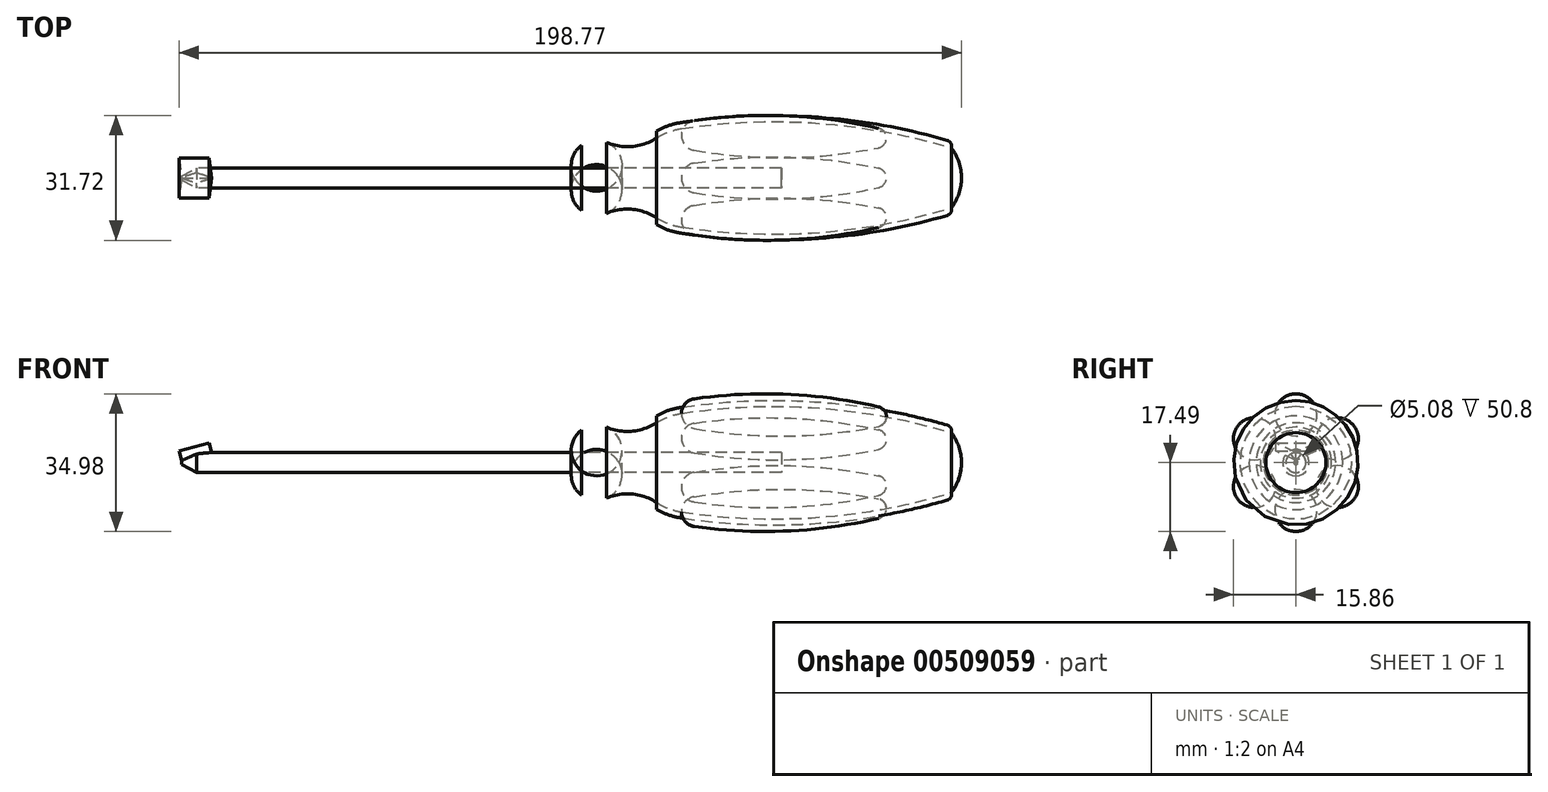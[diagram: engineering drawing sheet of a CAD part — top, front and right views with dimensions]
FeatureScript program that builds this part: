
annotation { "Feature Type Name" : "Feature", "Feature Type Description" : "" }
export const myFeature = defineFeature(function(context is Context, id is Id, definition is map)
    precondition{}
    {
        {
            var Q0;
            Q0=qCreatedBy(makeId("Front.planeOp"),FACE);
            var sketch = newSketch(context, id + "F0", { "sketchPlane" : qUnion([Q0])});
            skLineSegment(sketch, "E0", {"start": v(-101.6, 0) * mm, "end": v(96.52, 0) * mm});
            skLineSegment(sketch, "E1", {"start": v(96.52, 0) * mm, "end": v(117.55, 0) * mm, "construction": true});
            skLineSegment(sketch, "E2", {"start": v(50.8, 2.54) * mm, "end": v(-97.8, 2.54) * mm});
            skLineSegment(sketch, "E3", {"start": v(-101.6, 0.5) * mm, "end": v(-101.6, 0) * mm});
            skLineSegment(sketch, "E4", {"start": v(0, 2.54) * mm, "end": v(0, 8.25) * mm});
            skArc(sketch, "E5", {"start": v(6.35, 9.02) * mm, "mid": v(3.07, 9.48) * mm, "end": v(0, 8.25) * mm});
            skArc(sketch, "E6", {"start": v(6.35, 9.02) * mm, "mid": v(12.84, 7.99) * mm, "end": v(19.05, 10.11) * mm});
            skArc(sketch, "E7", {"start": v(25.4, 12.52) * mm, "mid": v(22.1, 11.65) * mm, "end": v(19.05, 10.11) * mm});
            skArc(sketch, "E8", {"start": v(93.98, 7.62) * mm, "mid": v(59.96, 13.9) * mm, "end": v(25.4, 12.52) * mm});
            skArc(sketch, "E9", {"start": v(96.52, 0) * mm, "mid": v(95.87, 4.02) * mm, "end": v(93.98, 7.62) * mm});
            skArc(sketch, "E10.0", {"start": v(25.17, 14.02) * mm, "mid": v(22.01, 13.24) * mm, "end": v(19.05, 11.9) * mm});
            skArc(sketch, "E10.1", {"start": v(92.95, 9.52) * mm, "mid": v(59.3, 15.46) * mm, "end": v(25.17, 14.02) * mm});
            skLineSegment(sketch, "E11", {"start": v(19.05, 11.9) * mm, "end": v(19.05, 10.11) * mm});
            skArc(sketch, "E12", {"start": v(93.98, 7.62) * mm, "mid": v(93.86, 8.78) * mm, "end": v(92.95, 9.52) * mm});
            skPoint(sketch, "E13.orphan", {"position": v(0, 0) * mm});
            skLineSegment(sketch, "E14", {"start": v(50.8, 2.54) * mm, "end": v(50.8, 0) * mm});
            skLineSegment(sketch, "E15", {"start": v(-101.6, 0.5) * mm, "end": v(-97.8, 2.54) * mm});
            skPoint(sketch, "E16.orphan", {"position": v(-101.6, 2.54) * mm});
            skSolve(sketch);
        }
        {
            var Q0;
            Q0=qCreatedBy(makeId("Front.planeOp"),FACE);
            var sketch = newSketch(context, id + "F1", { "sketchPlane" : qUnion([Q0])});
            skLineSegment(sketch, "E17", {"start": v(25.4, 12.52) * mm, "end": v(77.47, 11.64) * mm});
            skArc(sketch, "E18", {"start": v(28.67, 16.22) * mm, "mid": v(26.35, 14.97) * mm, "end": v(25.4, 12.52) * mm});
            skArc(sketch, "E19", {"start": v(77.47, 11.64) * mm, "mid": v(76.93, 13.25) * mm, "end": v(75.5, 14.16) * mm});
            skArc(sketch, "E20", {"start": v(75.5, 14.16) * mm, "mid": v(52.19, 17.37) * mm, "end": v(28.67, 16.22) * mm});
            skSolve(sketch);
        }
        {
            var Q0;
            Q0=qCreatedBy(makeId("Front.planeOp"),FACE);
            var sketch = newSketch(context, id + "F2", { "sketchPlane" : qUnion([Q0])});
            skLineSegment(sketch, "E21", {"start": v(-101.6, 0.5) * mm, "end": v(-93.98, 2.54) * mm});
            skSolve(sketch);
        }
        {
            var Q0;
            Q0=sQuery(id+"F2.wireOp",VERTEX,"E21.start");
            var Q1;
            Q1=sQuery(id+"F2.wireOp",EDGE,"E21");
            cPlane(context, id + "F3", {"entities" : qUnion([Q0, Q1]), "cplaneType" : CPlaneType.LINE_POINT, "offset" : 25.4 * mm, "width" : 152.4 * mm, "height" : 152.4 * mm});
        }
        {
            var Q0;
            Q0=qCreatedBy(id+"F3.planeOp",FACE);
            var sketch = newSketch(context, id + "F4", { "sketchPlane" : qUnion([Q0])});
            skLineSegment(sketch, "E22", {"start": v(5.08, 29.2) * mm, "end": v(0, 26.67) * mm});
            skLineSegment(sketch, "E23", {"start": v(0, 26.67) * mm, "end": v(-5.08, 29.2) * mm});
            skLineSegment(sketch, "E24", {"start": v(-5.08, 29.2) * mm, "end": v(5.08, 29.2) * mm});
            skLineSegment(sketch, "E25", {"start": v(0, 29.2) * mm, "end": v(0, 26.67) * mm, "construction": true});
            skSolve(sketch);
        }
        {
            var Q0;
            {var subQ0=sQuery(id+"F0.wireOp",EDGE,"E3");Q0=makeQuery(id+"F0.imprint","IMPRINT",FACE,{"disambiguationData":[TD([[makeQuery(id+"F0.imprint","IMPRINT",EDGE,{"derivedFrom":subQ0}),1.0]])]});}
            var Q1;
            Q1=sQuery(id+"F0.wireOp",EDGE,"E0");
            revolve(context, id + "F5", {"entities" : qUnion([Q0]), "axis" : qUnion([Q1]), "revolveType" : RevolveType.FULL});
        }
        {
            var Q0;
            {var subQ0=sQuery(id+"F0.wireOp",EDGE,"E4");Q0=makeQuery(id+"F0.imprint","IMPRINT",FACE,{"disambiguationData":[TD([[makeQuery(id+"F0.imprint","IMPRINT",EDGE,{"derivedFrom":subQ0}),-1.0]])]});}
            var Q1;
            Q1=sQuery(id+"F0.wireOp",EDGE,"E0");
            revolve(context, id + "F6", {"entities" : qUnion([Q0]), "axis" : qUnion([Q1]), "revolveType" : RevolveType.FULL});
        }
        {
            var Q0;
            Q0=makeQuery(id+"F0.imprint","IMPRINT",FACE,{"disambiguationData":[TD([[makeQuery(id+"F0.imprint","IMPRINT",EDGE,{"derivedFrom":sQuery(id+"F0.wireOp",EDGE,"E7")}),-1.0]])]});
            var Q1;
            Q1=sQuery(id+"F0.wireOp",EDGE,"E0");
            revolve(context, id + "F7", {"entities" : qUnion([Q0]), "axis" : qUnion([Q1]), "revolveType" : RevolveType.FULL});
        }
        {
            var Q0;
            Q0=makeQuery(id+"F1.imprint","IMPRINT",FACE,{"disambiguationData":[TD([[makeQuery(id+"F1.imprint","IMPRINT",EDGE,{"derivedFrom":sQuery(id+"F1.wireOp",EDGE,"E17")}),1.0]])]});
            var Q1;
            Q1=sQuery(id+"F1.wireOp",EDGE,"E17");
            revolve(context, id + "F8", {"entities" : qUnion([Q0]), "axis" : qUnion([Q1]), "revolveType" : RevolveType.FULL});
        }
        {
            var Q0;
            Q0=makeQuery(id+"F8.opRevolve","SWEPT_BODY",BODY,{"disambiguationData":[OSD([sQuery(id+"F1.wireOp",EDGE,"E17"),sQuery(id+"F1.wireOp",EDGE,"E18"),sQuery(id+"F1.wireOp",EDGE,"E19"),sQuery(id+"F1.wireOp",EDGE,"E20")])]});
            var Q1;
            Q1=sQuery(id+"F0.wireOp",EDGE,"E0");
            circularPattern(context, id + "F9", {"entities" : qUnion([Q0]), "axis" : qUnion([Q1]), "angle" : 360 * degree, "instanceCount" : 6, "equalSpace" : true, "computeTransformsWithoutBuiltin" : true});
        }
        {
            var Q0;
            Q0=makeQuery(id+"F5.opRevolve","SWEPT_BODY",BODY,{"disambiguationData":[OSD([sQuery(id+"F0.wireOp",EDGE,"E0"),sQuery(id+"F0.wireOp",EDGE,"E2"),sQuery(id+"F0.wireOp",EDGE,"E3"),sQuery(id+"F0.wireOp",EDGE,"E14"),sQuery(id+"F0.wireOp",EDGE,"E15")])]});
            var Q1;
            Q1=makeQuery(id+"F6.opRevolve","SWEPT_BODY",BODY,{"disambiguationData":[OSD([sQuery(id+"F0.wireOp",EDGE,"E0"),sQuery(id+"F0.wireOp",EDGE,"E2"),sQuery(id+"F0.wireOp",EDGE,"E4"),sQuery(id+"F0.wireOp",EDGE,"E5"),sQuery(id+"F0.wireOp",EDGE,"E6"),sQuery(id+"F0.wireOp",EDGE,"E7"),sQuery(id+"F0.wireOp",EDGE,"E8"),sQuery(id+"F0.wireOp",EDGE,"E9"),sQuery(id+"F0.wireOp",EDGE,"E14")])]});
            booleanBodies(context, id + "F10", {"operationType" : BooleanOperationType.SUBTRACTION, "tools" : qUnion([Q0]), "targets" : qUnion([Q1]), "keepTools" : true});
        }
        {
            var Q0;
            Q0=makeQuery(id+"F4.imprint","IMPRINT",FACE,{"disambiguationData":[TD([[makeQuery(id+"F4.imprint","IMPRINT",EDGE,{"derivedFrom":sQuery(id+"F4.wireOp",EDGE,"E22")}),-1.0]])]});
            var Q1;
            Q1 = qConstructionFilter(qBodyType(qCreatedBy(id + "F2" ,EDGE), BodyType.WIRE), ConstructionObject.NO);
            sweep(context, id + "F11", {"operationType" : NewBodyOperationType.REMOVE, "profiles" : qUnion([Q0]), "path" : qUnion([Q1])});
        }
        {
            var Q0;
            Q0=makeQuery(id+"F4.imprint","IMPRINT",FACE,{"disambiguationData":[TD([[makeQuery(id+"F4.imprint","IMPRINT",EDGE,{"derivedFrom":sQuery(id+"F4.wireOp",EDGE,"E22")}),-1.0]])]});
            var Q1;
            Q1=qConstructionFilter(qBodyType(qCreatedBy(id+"F2",EDGE),BodyType.WIRE),ConstructionObject.NO);
            sweep(context, id + "F12", {"profiles" : qUnion([Q0]), "path" : qUnion([Q1])});
        }
    });
